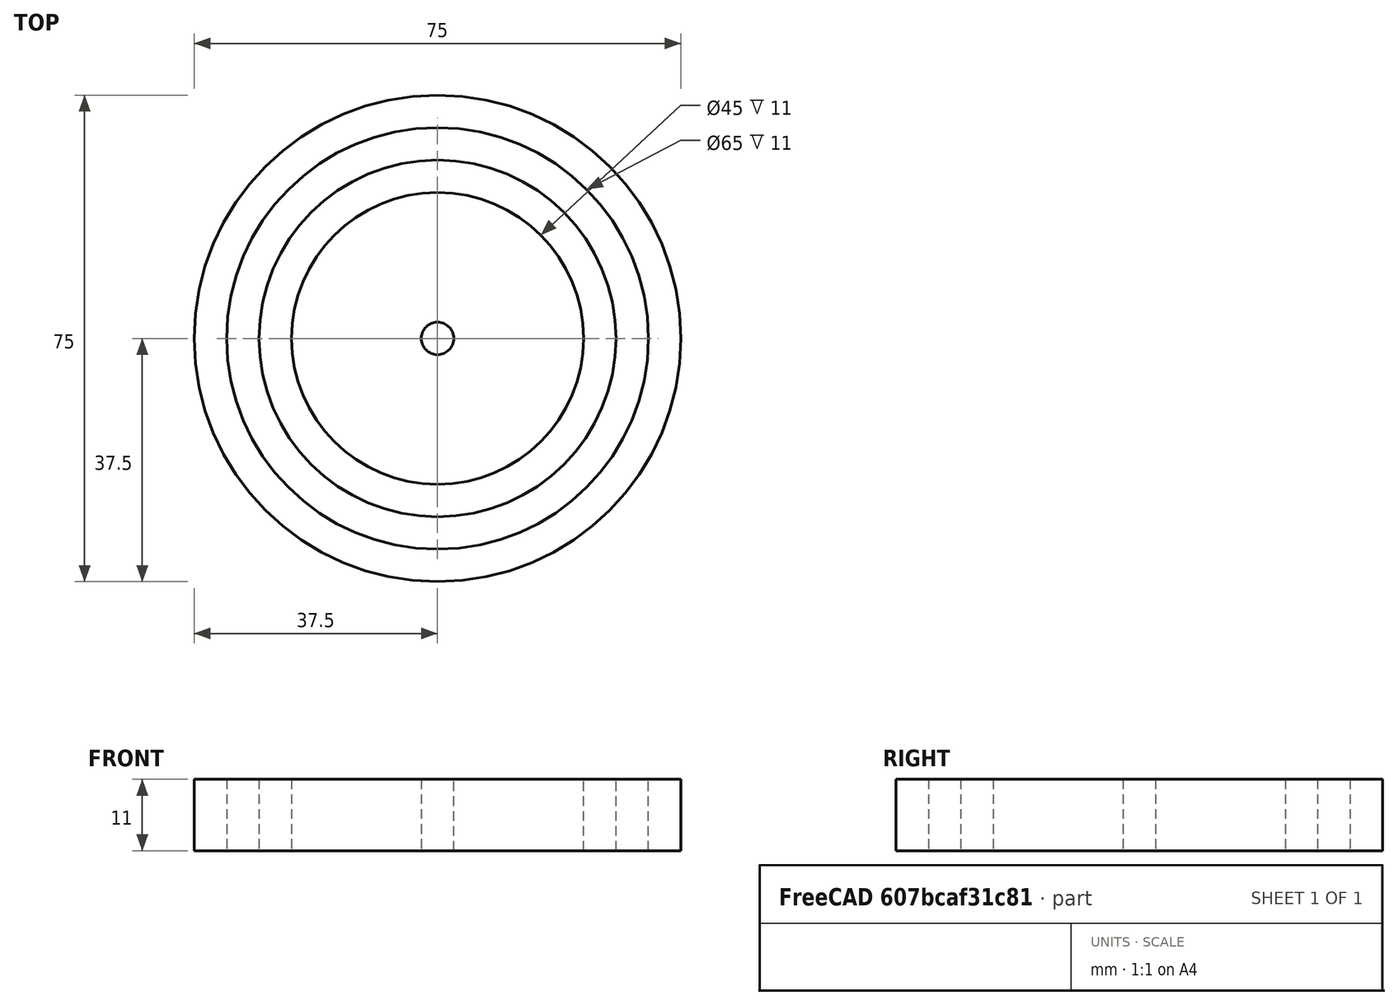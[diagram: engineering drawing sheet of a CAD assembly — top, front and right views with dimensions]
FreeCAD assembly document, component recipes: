
FREECAD ASSEMBLY — COMPONENT RECIPES ("Assambly_bearing_45x75x11")

This assembly document has 4 components, labeled P0..P3 below (a component is one placed body or linked part). 3 of them carry a construction recipe — the FreeCAD feature program that regenerates the part from scratch, quoted from this document or its linked companion documents; the rest are supplied as boundary geometry only. No exploded tour is included for this assembly.
COMPONENT P0 — geometry summary ("Assembly"; no construction recipe available for this part):
  bounding box: 75.0 x 75.0 x 11.0 mm
  tessellated surface: 208 triangles
  volume: 1188571428571428608091837590807025526931679251701097734487443175340447316937393037983811611623744864256 mm^3 (1920923520923521277903375288930195059977532918160605994139290579784343134719611399500306134809444352% of its bounding box)
  symmetry: 2-fold rotationally symmetric about the x axis; 2-fold rotationally symmetric about the y axis; 4-fold rotationally symmetric about the z axis; mirror-symmetric across its x mid-plane, y mid-plane, z mid-plane
COMPONENT P1 — recipe-attached ("Body_roller", modeled in this document).
Construction recipe (the document's own serialized feature program — sketch geometry with constraints, then the solid features built on it; lengths are millimeters unless a unit is written):

FEATURE [Sketcher::SketchObject] Sketch
  FullyConstrained = true
  MapMode = 5
  Support = -> [XY_Plane005]
  sketch-geometry (1):
    g0: Circle CenterX=0 CenterY=0 CenterZ=0 NormalX=0 NormalY=0 NormalZ=1 AngleXU=0 Radius=2.5
  constraints (2):
    c: Diameter(g0) = 5
    c: Coincident(g0,g-1)
FEATURE [PartDesign::Pad] Pad
  Direction = (1,1,1)
  Length = 11
  Length2 = 100
  Profile = -> Sketch
  Type = 0
FEATURE [PartDesign::CoordinateSystem] LCS_Roller
  AttacherType = Attacher::AttachEngine3D
  MapMode = 11
  Placement = pos=(0,0,11) rot=(0,0,1;1.5708rad)
  Support = -> [Pad]
FEATURE [PartDesign::Body] Body  label="Body_roller"
  Group = -> [Sketch,Pad,LCS_Roller]
  Origin = -> Origin001
  Tip = -> Pad
COMPONENT P2 — recipe-attached ("Body_ring_in", modeled in this document).
Construction recipe (the document's own serialized feature program — sketch geometry with constraints, then the solid features built on it; lengths are millimeters unless a unit is written):

FEATURE [Sketcher::SketchObject] Sketch004
  FullyConstrained = true
  MapMode = 5
  Support = -> [XY_Plane006]
  sketch-geometry (2):
    g0: Circle CenterX=0 CenterY=0 CenterZ=0 NormalX=0 NormalY=0 NormalZ=1 AngleXU=0 Radius=27.5
    g1: Circle CenterX=0 CenterY=0 CenterZ=0 NormalX=0 NormalY=0 NormalZ=1 AngleXU=0 Radius=22.5
  constraints (4):
    c: Coincident(g1,g0)
    c: Diameter(g1) = 45
    c: Diameter(g0) = 55
    c: Coincident(g0,g-1)
FEATURE [PartDesign::Pad] Pad001
  Direction = (1,1,1)
  Length = 11
  Length2 = 100
  Profile = -> Sketch004
  Type = 0
FEATURE [PartDesign::CoordinateSystem] LCS_Ring_in
  AttacherType = Attacher::AttachEngine3D
  MapMode = 11
  Placement = pos=(0,0,11) rot=(0,0,1;1.5708rad)
  Support = -> [Pad001]
FEATURE [PartDesign::Body] Body001  label="Body_ring_in"
  Group = -> [Sketch004,Pad001,LCS_Ring_in]
  Origin = -> Origin002
  Tip = -> Pad001
COMPONENT P3 — recipe-attached ("Body_ring_out", modeled in this document).
Construction recipe (the document's own serialized feature program — sketch geometry with constraints, then the solid features built on it; lengths are millimeters unless a unit is written):

FEATURE [Sketcher::SketchObject] Sketch005
  FullyConstrained = true
  MapMode = 5
  Support = -> [XY_Plane007]
  sketch-geometry (2):
    g0: Circle CenterX=0 CenterY=0 CenterZ=0 NormalX=0 NormalY=0 NormalZ=1 AngleXU=0 Radius=32.5
    g1: Circle CenterX=0 CenterY=0 CenterZ=0 NormalX=0 NormalY=0 NormalZ=1 AngleXU=0 Radius=37.5
  constraints (4):
    c: Coincident(g1,g0)
    c: Diameter(g1) = 75
    c: Diameter(g0) = 65
    c: Coincident(g0,g-1)
FEATURE [PartDesign::Pad] Pad002
  Direction = (1,1,1)
  Length = 11
  Length2 = 100
  Profile = -> Sketch005
  Type = 0
FEATURE [PartDesign::CoordinateSystem] LCS_Ring_out
  AttacherType = Attacher::AttachEngine3D
  MapMode = 11
  Placement = pos=(0,0,11) rot=(0,0,1;1.5708rad)
  Support = -> [Pad002]
FEATURE [PartDesign::Body] Body002  label="Body_ring_out"
  Group = -> [Sketch005,Pad002,LCS_Ring_out]
  Origin = -> Origin003
  Tip = -> Pad002
PROVENANCE & LICENSES
A FreeCAD (.FCStd) document from a public repository crawl; recipes are the document's own serialized feature recipes (and, for linked parts, companion documents' recipes).
License: as declared in the source repository (recorded in the dataset sidecar).
